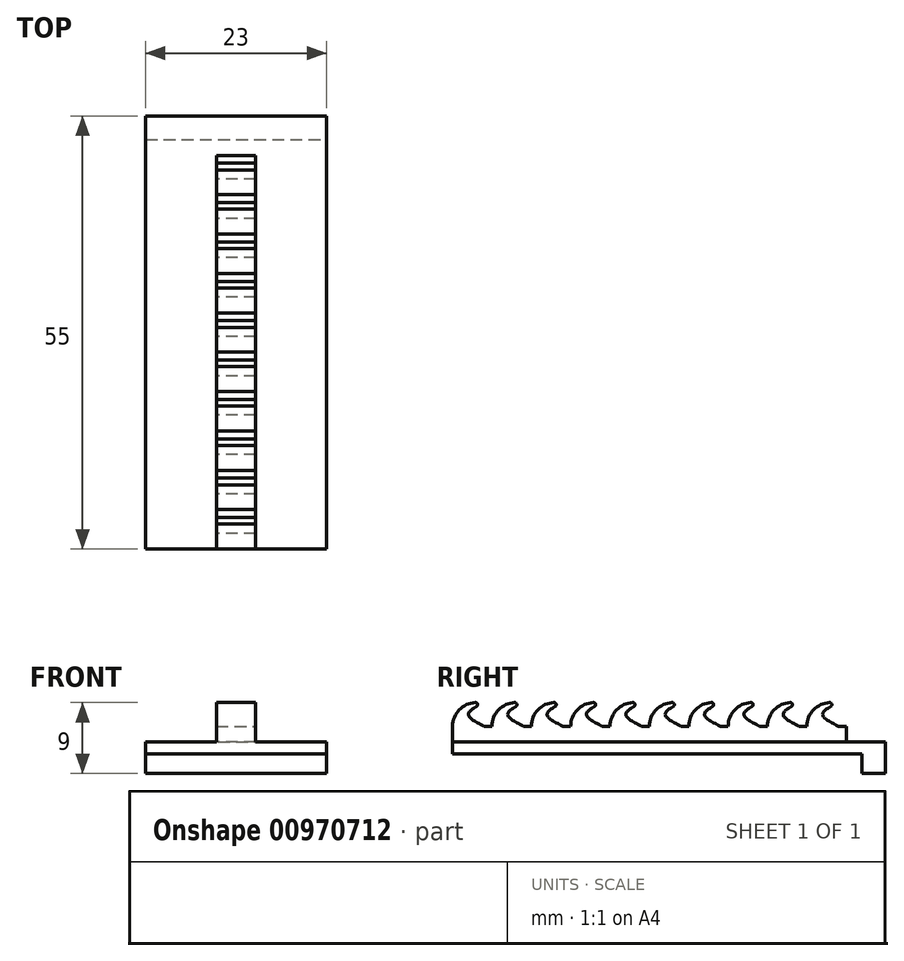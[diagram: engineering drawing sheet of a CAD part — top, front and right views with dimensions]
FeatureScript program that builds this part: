
annotation { "Feature Type Name" : "Feature", "Feature Type Description" : "" }
export const myFeature = defineFeature(function(context is Context, id is Id, definition is map)
    precondition{}
    {
        {
            var Q0;
            Q0=qCreatedBy(makeId("Top.planeOp"),FACE);
            var sketch = newSketch(context, id + "F0", { "sketchPlane" : qUnion([Q0])});
            skLineSegment(sketch, "E0.bottom", {"start": v(-13.13, 25.1) * mm, "end": v(9.87, 25.1) * mm});
            skLineSegment(sketch, "E0.top", {"start": v(-13.13, -26.9) * mm, "end": v(9.87, -26.9) * mm});
            skLineSegment(sketch, "E0.left", {"start": v(-13.13, 25.1) * mm, "end": v(-13.13, -26.9) * mm});
            skLineSegment(sketch, "E0.right", {"start": v(9.87, 25.1) * mm, "end": v(9.87, -26.9) * mm});
            skSolve(sketch);
        }
        {
            var Q0;
            Q0=makeQuery(id+"F0.imprint","IMPRINT",FACE,{"disambiguationData":[TD([[makeQuery(id+"F0.imprint","IMPRINT",EDGE,{"derivedFrom":sQuery(id+"F0.wireOp",EDGE,"E0.bottom")}),-1.0]])]});
            extrude(context, id + "F1", {"entities" : qUnion([Q0]), "depth" : 1.5 * mm, "offsetDistance" : 25 * mm});
        }
        {
            var Q0;
            Q0=makeQuery(id+"F1.opExtrude","SWEPT_FACE",FACE,{"disambiguationData":[OSD([sQuery(id+"F0.wireOp",EDGE,"E0.bottom")])]});
            var sketch = newSketch(context, id + "F2", { "sketchPlane" : qUnion([Q0])});
            skLineSegment(sketch, "E1.bottom", {"start": v(-9.87, 1.5) * mm, "end": v(13.13, 1.5) * mm});
            skLineSegment(sketch, "E1.top", {"start": v(-9.87, -2.5) * mm, "end": v(13.13, -2.5) * mm});
            skLineSegment(sketch, "E1.left", {"start": v(-9.87, 1.5) * mm, "end": v(-9.87, -2.5) * mm});
            skLineSegment(sketch, "E1.right", {"start": v(13.13, 1.5) * mm, "end": v(13.13, -2.5) * mm});
            skSolve(sketch);
        }
        {
            var Q0;
            Q0 = qSketchRegion(id + "F2", true);
            extrude(context, id + "F3", {"entities" : qUnion([Q0]), "operationType" : NewBodyOperationType.ADD, "depth" : 3 * mm, "offsetDistance" : 25 * mm});
        }
        {
            var Q0;
            Q0=makeQuery(id+"F3.boolean.opBoolean","MERGE",FACE,{"derivedFrom":[makeQuery(id+"F1.opExtrude","CAP_FACE",FACE,{"disambiguationData":[OSD([sQuery(id+"F0.wireOp",EDGE,"E0.bottom"),sQuery(id+"F0.wireOp",EDGE,"E0.top"),sQuery(id+"F0.wireOp",EDGE,"E0.left"),sQuery(id+"F0.wireOp",EDGE,"E0.right")])],"isStart":false}),makeQuery(id+"F3.opExtrude","SWEPT_FACE",FACE,{"disambiguationData":[OSD([sQuery(id+"F2.wireOp",EDGE,"E1.bottom")])]})]});
            var sketch = newSketch(context, id + "F4", { "sketchPlane" : qUnion([Q0])});
            skLineSegment(sketch, "E2", {"start": v(-1.63, -26.9) * mm, "end": v(-4.13, -26.9) * mm});
            skLineSegment(sketch, "E3", {"start": v(-1.63, -26.9) * mm, "end": v(0.87, -26.9) * mm});
            skLineSegment(sketch, "E4.bottom", {"start": v(-4.13, -26.9) * mm, "end": v(0, -26.9) * mm});
            skLineSegment(sketch, "E4.left", {"start": v(-4.13, -26.9) * mm, "end": v(-4.13, 23.1) * mm});
            skLineSegment(sketch, "E5", {"start": v(0.87, -26.9) * mm, "end": v(0.87, 23.1) * mm});
            skLineSegment(sketch, "E6", {"start": v(0.87, 23.1) * mm, "end": v(-4.13, 23.1) * mm});
            skSolve(sketch);
        }
        {
            var Q0;
            Q0 = qSketchRegion(id + "F4", true);
            extrude(context, id + "F5", {"entities" : qUnion([Q0]), "operationType" : NewBodyOperationType.ADD, "depth" : 2 * mm, "offsetDistance" : 25 * mm});
        }
        {
            var Q0;
            Q0=makeQuery(id+"F5.opExtrude","CAP_FACE",FACE,{"disambiguationData":[OSD([sQuery(id+"F4.wireOp",EDGE,"E4.bottom"),sQuery(id+"F4.wireOp",EDGE,"E4.top"),sQuery(id+"F4.wireOp",EDGE,"E4.left"),sQuery(id+"F4.wireOp",EDGE,"E4.right")])],"isStart":false});
            var sketch = newSketch(context, id + "F6", { "sketchPlane" : qUnion([Q0])});
            skLineSegment(sketch, "E7.bottom", {"start": v(-4.13, -26.9) * mm, "end": v(0.87, -26.9) * mm});
            skLineSegment(sketch, "E7.top", {"start": v(-4.13, -21.9) * mm, "end": v(0.87, -21.9) * mm});
            skLineSegment(sketch, "E7.left", {"start": v(-4.13, -26.9) * mm, "end": v(-4.13, -21.9) * mm});
            skLineSegment(sketch, "E7.right", {"start": v(0.87, -26.9) * mm, "end": v(0.87, -21.9) * mm});
            skLineSegment(sketch, "E8.top", {"start": v(-4.13, -16.9) * mm, "end": v(0.87, -16.9) * mm});
            skLineSegment(sketch, "E8.left", {"start": v(-4.13, -21.9) * mm, "end": v(-4.13, -16.9) * mm});
            skLineSegment(sketch, "E8.right", {"start": v(0.87, -21.9) * mm, "end": v(0.87, -16.9) * mm});
            skLineSegment(sketch, "E9", {"start": v(0.87, -16.9) * mm, "end": v(0.87, -11.9) * mm});
            skLineSegment(sketch, "E10", {"start": v(0.87, -11.9) * mm, "end": v(0.87, -6.9) * mm});
            skPoint(sketch, "E11", {"position": v(0.87, -1.9) * mm});
            skPoint(sketch, "E12", {"position": v(0.87, 3.1) * mm});
            skPoint(sketch, "E13", {"position": v(0.87, 8.1) * mm});
            skPoint(sketch, "E14", {"position": v(0.87, 13.1) * mm});
            skPoint(sketch, "E15", {"position": v(0.87, 18.1) * mm});
            skPoint(sketch, "E16", {"position": v(0.87, 23.1) * mm});
            skLineSegment(sketch, "E17.top", {"start": v(-4.13, -11.9) * mm, "end": v(0.87, -11.9) * mm});
            skLineSegment(sketch, "E17.left", {"start": v(-4.13, -16.9) * mm, "end": v(-4.13, -11.9) * mm});
            skLineSegment(sketch, "E18.top", {"start": v(-4.13, -6.9) * mm, "end": v(0.87, -6.9) * mm});
            skLineSegment(sketch, "E18.left", {"start": v(-4.13, -11.9) * mm, "end": v(-4.13, -6.9) * mm});
            skLineSegment(sketch, "E19.top", {"start": v(-4.13, -1.9) * mm, "end": v(0.87, -1.9) * mm});
            skLineSegment(sketch, "E19.left", {"start": v(-4.13, -6.9) * mm, "end": v(-4.13, -1.9) * mm});
            skLineSegment(sketch, "E19.right", {"start": v(0.87, -6.9) * mm, "end": v(0.87, -1.9) * mm});
            skLineSegment(sketch, "E20.top", {"start": v(-4.13, 3.1) * mm, "end": v(0.87, 3.1) * mm});
            skLineSegment(sketch, "E20.left", {"start": v(-4.13, -1.9) * mm, "end": v(-4.13, 3.1) * mm});
            skLineSegment(sketch, "E20.right", {"start": v(0.87, -1.9) * mm, "end": v(0.87, 3.1) * mm});
            skLineSegment(sketch, "E21.top", {"start": v(-4.13, 8.1) * mm, "end": v(0.87, 8.1) * mm});
            skLineSegment(sketch, "E21.left", {"start": v(-4.13, 3.1) * mm, "end": v(-4.13, 8.1) * mm});
            skLineSegment(sketch, "E21.right", {"start": v(0.87, 3.1) * mm, "end": v(0.87, 8.1) * mm});
            skLineSegment(sketch, "E22.top", {"start": v(-4.13, 13.1) * mm, "end": v(0.87, 13.1) * mm});
            skLineSegment(sketch, "E22.left", {"start": v(-4.13, 8.1) * mm, "end": v(-4.13, 13.1) * mm});
            skLineSegment(sketch, "E22.right", {"start": v(0.87, 8.1) * mm, "end": v(0.87, 13.1) * mm});
            skLineSegment(sketch, "E23.top", {"start": v(-4.13, 18.1) * mm, "end": v(0.87, 18.1) * mm});
            skLineSegment(sketch, "E23.left", {"start": v(-4.13, 13.1) * mm, "end": v(-4.13, 18.1) * mm});
            skLineSegment(sketch, "E23.right", {"start": v(0.87, 13.1) * mm, "end": v(0.87, 18.1) * mm});
            skLineSegment(sketch, "E24.top", {"start": v(-4.13, 23.1) * mm, "end": v(0.87, 23.1) * mm});
            skLineSegment(sketch, "E24.left", {"start": v(-4.13, 18.1) * mm, "end": v(-4.13, 23.1) * mm});
            skLineSegment(sketch, "E24.right", {"start": v(0.87, 18.1) * mm, "end": v(0.87, 23.1) * mm});
            skLineSegment(sketch, "E25", {"start": v(-4.13, -22.9) * mm, "end": v(0.87, -22.9) * mm});
            skLineSegment(sketch, "E26", {"start": v(-4.13, -17.9) * mm, "end": v(0.87, -17.9) * mm});
            skLineSegment(sketch, "E27", {"start": v(-4.13, 22.1) * mm, "end": v(0.87, 22.1) * mm});
            skLineSegment(sketch, "E28", {"start": v(-4.13, 17.1) * mm, "end": v(0.87, 17.1) * mm});
            skLineSegment(sketch, "E29", {"start": v(0.87, 17.1) * mm, "end": v(0.87, 12.1) * mm});
            skLineSegment(sketch, "E30", {"start": v(0.87, 12.1) * mm, "end": v(-4.13, 12.1) * mm});
            skLineSegment(sketch, "E31", {"start": v(-4.13, 12.1) * mm, "end": v(-4.13, 7.1) * mm});
            skLineSegment(sketch, "E32", {"start": v(-4.13, 7.1) * mm, "end": v(0.87, 7.1) * mm});
            skLineSegment(sketch, "E33", {"start": v(0.87, 7.1) * mm, "end": v(0.87, 2.1) * mm});
            skLineSegment(sketch, "E34", {"start": v(0.87, 2.1) * mm, "end": v(-4.13, 2.1) * mm});
            skLineSegment(sketch, "E35", {"start": v(-4.13, 2.1) * mm, "end": v(-4.13, -2.9) * mm});
            skLineSegment(sketch, "E36", {"start": v(-4.13, -2.9) * mm, "end": v(0.87, -2.9) * mm});
            skLineSegment(sketch, "E37", {"start": v(0.87, 2.1) * mm, "end": v(0.87, -2.9) * mm});
            skLineSegment(sketch, "E38", {"start": v(0.87, -2.9) * mm, "end": v(0.87, -7.9) * mm});
            skLineSegment(sketch, "E39", {"start": v(0.87, -7.9) * mm, "end": v(-4.13, -7.9) * mm});
            skLineSegment(sketch, "E40", {"start": v(-4.13, -7.9) * mm, "end": v(-4.13, -12.9) * mm});
            skLineSegment(sketch, "E41", {"start": v(-4.13, -12.9) * mm, "end": v(0.87, -12.9) * mm});
            skSolve(sketch);
        }
        {
            var Q0;
            {var subQ0=sQuery(id+"F6.wireOp",EDGE,"E7.bottom");Q0=makeQuery(id+"F6.imprint","IMPRINT",FACE,{"disambiguationData":[TD([[makeQuery(id+"F6.imprint","IMPRINT",EDGE,{"derivedFrom":subQ0}),1.0]])]});}
            var Q1;
            {var subQ0=sQuery(id+"F6.wireOp",EDGE,"E7.top");Q1=makeQuery(id+"F6.imprint","IMPRINT",FACE,{"disambiguationData":[TD([[makeQuery(id+"F6.imprint","IMPRINT",EDGE,{"derivedFrom":subQ0}),1.0]])]});}
            var Q2;
            {var subQ0=sQuery(id+"F6.wireOp",EDGE,"E8.top");Q2=makeQuery(id+"F6.imprint","IMPRINT",FACE,{"disambiguationData":[TD([[makeQuery(id+"F6.imprint","IMPRINT",EDGE,{"derivedFrom":subQ0}),1.0]])]});}
            var Q3;
            {var subQ0=sQuery(id+"F6.wireOp",EDGE,"E17.top");Q3=makeQuery(id+"F6.imprint","IMPRINT",FACE,{"disambiguationData":[TD([[makeQuery(id+"F6.imprint","IMPRINT",EDGE,{"derivedFrom":subQ0}),1.0]])]});}
            var Q4;
            {var subQ0=sQuery(id+"F6.wireOp",EDGE,"E18.top");Q4=makeQuery(id+"F6.imprint","IMPRINT",FACE,{"disambiguationData":[TD([[makeQuery(id+"F6.imprint","IMPRINT",EDGE,{"derivedFrom":subQ0}),1.0]])]});}
            var Q5;
            {var subQ0=sQuery(id+"F6.wireOp",EDGE,"E19.top");Q5=makeQuery(id+"F6.imprint","IMPRINT",FACE,{"disambiguationData":[TD([[makeQuery(id+"F6.imprint","IMPRINT",EDGE,{"derivedFrom":subQ0}),1.0]])]});}
            var Q6;
            {var subQ0=sQuery(id+"F6.wireOp",EDGE,"E20.top");Q6=makeQuery(id+"F6.imprint","IMPRINT",FACE,{"disambiguationData":[TD([[makeQuery(id+"F6.imprint","IMPRINT",EDGE,{"derivedFrom":subQ0}),1.0]])]});}
            var Q7;
            {var subQ0=sQuery(id+"F6.wireOp",EDGE,"E19.top");Q7=makeQuery(id+"F6.imprint","IMPRINT",FACE,{"disambiguationData":[TD([[makeQuery(id+"F6.imprint","IMPRINT",EDGE,{"derivedFrom":subQ0}),1.0]])]});}
            var Q8;
            {var subQ0=sQuery(id+"F6.wireOp",EDGE,"E20.top");Q8=makeQuery(id+"F6.imprint","IMPRINT",FACE,{"disambiguationData":[TD([[makeQuery(id+"F6.imprint","IMPRINT",EDGE,{"derivedFrom":subQ0}),1.0]])]});}
            var Q9;
            {var subQ0=sQuery(id+"F6.wireOp",EDGE,"E21.top");Q9=makeQuery(id+"F6.imprint","IMPRINT",FACE,{"disambiguationData":[TD([[makeQuery(id+"F6.imprint","IMPRINT",EDGE,{"derivedFrom":subQ0}),1.0]])]});}
            var Q10;
            {var subQ0=sQuery(id+"F6.wireOp",EDGE,"E22.top");Q10=makeQuery(id+"F6.imprint","IMPRINT",FACE,{"disambiguationData":[TD([[makeQuery(id+"F6.imprint","IMPRINT",EDGE,{"derivedFrom":subQ0}),1.0]])]});}
            var Q11;
            {var subQ0=sQuery(id+"F6.wireOp",EDGE,"E23.top");Q11=makeQuery(id+"F6.imprint","IMPRINT",FACE,{"disambiguationData":[TD([[makeQuery(id+"F6.imprint","IMPRINT",EDGE,{"derivedFrom":subQ0}),1.0]])]});}
            extrude(context, id + "F7", {"entities" : qUnion([Q0, Q1, Q2, Q3, Q4, Q5, Q6, Q7, Q8, Q9, Q10, Q11]), "operationType" : NewBodyOperationType.ADD, "depth" : 3 * mm, "offsetDistance" : 25 * mm});
        }
        {
            var Q0;
            Q0=makeQuery(id+"F7.boolean.opBoolean","MERGE",FACE,{"derivedFrom":[makeQuery(id+"F5.opExtrude","SWEPT_FACE",FACE,{"disambiguationData":[OSD([sQuery(id+"F4.wireOp",EDGE,"E4.left")])]}),makeQuery(id+"F7.opExtrude","SWEPT_FACE",FACE,{"disambiguationData":[OSD([sQuery(id+"F6.wireOp",EDGE,"E7.left")])]}),makeQuery(id+"F7.opExtrude","SWEPT_FACE",FACE,{"disambiguationData":[OSD([sQuery(id+"F6.wireOp",EDGE,"E8.left")])]}),makeQuery(id+"F7.opExtrude","SWEPT_FACE",FACE,{"disambiguationData":[OSD([sQuery(id+"F6.wireOp",EDGE,"E17.left")])]}),makeQuery(id+"F7.opExtrude","SWEPT_FACE",FACE,{"disambiguationData":[OSD([sQuery(id+"F6.wireOp",EDGE,"E18.left")])]}),makeQuery(id+"F7.opExtrude","SWEPT_FACE",FACE,{"disambiguationData":[OSD([sQuery(id+"F6.wireOp",EDGE,"E19.left")])]}),makeQuery(id+"F7.opExtrude","SWEPT_FACE",FACE,{"disambiguationData":[OSD([sQuery(id+"F6.wireOp",EDGE,"E20.left")])]}),makeQuery(id+"F7.opExtrude","SWEPT_FACE",FACE,{"disambiguationData":[OSD([sQuery(id+"F6.wireOp",EDGE,"E21.left")])]}),makeQuery(id+"F7.opExtrude","SWEPT_FACE",FACE,{"disambiguationData":[OSD([sQuery(id+"F6.wireOp",EDGE,"E22.left")])]}),makeQuery(id+"F7.opExtrude","SWEPT_FACE",FACE,{"disambiguationData":[OSD([sQuery(id+"F6.wireOp",EDGE,"E23.left")])]}),makeQuery(id+"F7.opExtrude","SWEPT_FACE",FACE,{"disambiguationData":[OSD([sQuery(id+"F6.wireOp",EDGE,"E24.left")])]})]});
            var sketch = newSketch(context, id + "F8", { "sketchPlane" : qUnion([Q0])});
            skPoint(sketch, "E42", {"position": v(24.9, 5) * mm});
            skPoint(sketch, "E42.positionSnap0", {"position": v(24.9, 6.5) * mm});
            skPoint(sketch, "E42.positionSnap1", {"position": v(22.9, 5) * mm});
            skFitSpline(sketch, "E43", {"points": [v(22.9, 3.5) * mm, v(24.9, 5) * mm, v(22.9, 6.5) * mm], "startDerivative": vector(6, 3) * mm, "endDerivative": vector(-6, 3) * mm});
            skPoint(sketch, "E44", {"position": v(17.9, 5) * mm});
            skPoint(sketch, "E45", {"position": v(19.9, 5) * mm});
            skPoint(sketch, "E45.positionSnap0", {"position": v(19.9, 6.5) * mm});
            skPoint(sketch, "E46", {"position": v(14.9, 5) * mm});
            skPoint(sketch, "E46.positionSnap0", {"position": v(14.9, 6.5) * mm});
            skPoint(sketch, "E46.positionSnap1", {"position": v(12.9, 5) * mm});
            skPoint(sketch, "E47", {"position": v(7.9, 5) * mm});
            skPoint(sketch, "E48", {"position": v(9.9, 5) * mm});
            skPoint(sketch, "E48.positionSnap0", {"position": v(9.9, 6.5) * mm});
            skPoint(sketch, "E49", {"position": v(4.9, 5) * mm});
            skPoint(sketch, "E49.positionSnap0", {"position": v(4.9, 6.5) * mm});
            skPoint(sketch, "E49.positionSnap1", {"position": v(2.9, 5) * mm});
            skPoint(sketch, "E50", {"position": v(-0.1, 5) * mm});
            skPoint(sketch, "E50.positionSnap0", {"position": v(-2.1, 5) * mm});
            skPoint(sketch, "E50.positionSnap1", {"position": v(-0.1, 6.5) * mm});
            skPoint(sketch, "E51", {"position": v(-5.1, 5) * mm});
            skPoint(sketch, "E51.positionSnap0", {"position": v(-5.1, 6.5) * mm});
            skPoint(sketch, "E51.positionSnap1", {"position": v(1.9, 5) * mm});
            skPoint(sketch, "E52.positionSnap1", {"position": v(-7.1, 5) * mm});
            skPoint(sketch, "E53", {"position": v(-10.1, 5) * mm});
            skPoint(sketch, "E53.positionSnap0", {"position": v(-10.1, 6.5) * mm});
            skPoint(sketch, "E53.positionSnap1", {"position": v(-12.1, 5) * mm});
            skPoint(sketch, "E54", {"position": v(-20.1, 5) * mm});
            skPoint(sketch, "E54.positionSnap0", {"position": v(-20.1, 6.5) * mm});
            skPoint(sketch, "E54.positionSnap1", {"position": v(-22.1, 5) * mm});
            skPoint(sketch, "E55", {"position": v(-15.1, 5) * mm});
            skPoint(sketch, "E55.positionSnap0", {"position": v(-15.1, 6.5) * mm});
            skPoint(sketch, "E55.positionSnap1", {"position": v(-17.1, 5) * mm});
            skFitSpline(sketch, "E56", {"points": [v(17.9, 3.5) * mm, v(19.9, 5) * mm, v(17.9, 6.5) * mm], "startDerivative": vector(6, 3) * mm, "endDerivative": vector(-6, 3) * mm});
            skFitSpline(sketch, "E57", {"points": [v(12.9, 3.5) * mm, v(14.9, 5) * mm, v(12.9, 6.5) * mm], "startDerivative": vector(6, 3) * mm, "endDerivative": vector(-6, 3) * mm});
            skFitSpline(sketch, "E58", {"points": [v(7.9, 3.5) * mm, v(9.9, 5) * mm, v(7.9, 6.5) * mm], "startDerivative": vector(6, 3) * mm, "endDerivative": vector(-6, 3) * mm});
            skFitSpline(sketch, "E59", {"points": [v(2.9, 3.5) * mm, v(4.9, 5) * mm, v(2.9, 6.5) * mm], "startDerivative": vector(6, 3) * mm, "endDerivative": vector(-6, 3) * mm});
            skFitSpline(sketch, "E60", {"points": [v(-2.1, 3.5) * mm, v(-0.1, 5) * mm, v(-2.1, 6.5) * mm], "startDerivative": vector(6, 3) * mm, "endDerivative": vector(-6, 3) * mm});
            skFitSpline(sketch, "E61", {"points": [v(-2.1, 3.5) * mm, v(-0.1, 5) * mm, v(-2.1, 6.5) * mm], "startDerivative": vector(6, 3) * mm, "endDerivative": vector(-6, 3) * mm});
            skFitSpline(sketch, "E62", {"points": [v(-7.1, 3.5) * mm, v(-5.1, 5) * mm, v(-7.1, 6.5) * mm], "startDerivative": vector(6, 3) * mm, "endDerivative": vector(-6, 3) * mm});
            skFitSpline(sketch, "E63", {"points": [v(-12.1, 3.5) * mm, v(-10.1, 5) * mm, v(-12.1, 6.5) * mm], "startDerivative": vector(6, 3) * mm, "endDerivative": vector(-6, 3) * mm});
            skFitSpline(sketch, "E64", {"points": [v(-17.1, 3.5) * mm, v(-15.1, 5) * mm, v(-17.1, 6.5) * mm], "startDerivative": vector(6, 3) * mm, "endDerivative": vector(-6, 3) * mm});
            skFitSpline(sketch, "E65", {"points": [v(-22.1, 3.5) * mm, v(-20.1, 5) * mm, v(-22.1, 6.5) * mm], "startDerivative": vector(6, 3) * mm, "endDerivative": vector(-6, 3) * mm});
            skLineSegment(sketch, "E66", {"start": v(-22.1, 3.5) * mm, "end": v(-22.1, 6.5) * mm});
            skLineSegment(sketch, "E67", {"start": v(-17.1, 3.5) * mm, "end": v(-17.1, 6.5) * mm});
            skLineSegment(sketch, "E68", {"start": v(-12.1, 3.5) * mm, "end": v(-12.1, 6.5) * mm});
            skLineSegment(sketch, "E69", {"start": v(-7.1, 3.5) * mm, "end": v(-7.1, 6.5) * mm});
            skLineSegment(sketch, "E70", {"start": v(-2.1, 3.5) * mm, "end": v(-2.1, 6.5) * mm});
            skLineSegment(sketch, "E71", {"start": v(1.9, 3.5) * mm, "end": v(1.9, 6.5) * mm});
            skLineSegment(sketch, "E72", {"start": v(2.9, 3.5) * mm, "end": v(2.9, 6.5) * mm});
            skLineSegment(sketch, "E73", {"start": v(7.9, 3.5) * mm, "end": v(7.9, 6.5) * mm});
            skLineSegment(sketch, "E74", {"start": v(12.9, 3.5) * mm, "end": v(12.9, 6.5) * mm});
            skLineSegment(sketch, "E75", {"start": v(17.9, 3.5) * mm, "end": v(17.9, 6.5) * mm});
            skLineSegment(sketch, "E76", {"start": v(22.9, 3.5) * mm, "end": v(22.9, 6.5) * mm});
            skSolve(sketch);
        }
        {
            var Q0;
            Q0 = qSketchRegion(id + "F8", true);
            var Q1;
            Q1=makeQuery(id+"F8.imprint","IMPRINT",FACE,{"disambiguationData":[TD([[makeQuery(id+"F8.imprint","IMPRINT",EDGE,{"derivedFrom":sQuery(id+"F8.wireOp",EDGE,"E43")}),1.0]])]});
            extrude(context, id + "F9", {"entities" : qUnion([Q0, Q1]), "operationType" : NewBodyOperationType.REMOVE, "oppositeDirection" : true, "depth" : 5.1 * mm, "offsetDistance" : 25 * mm});
        }
        {
            var Q0;
            Q0=makeQuery(id+"F7.opExtrude","CAP_EDGE",EDGE,{"disambiguationData":[OSD([sQuery(id+"F6.wireOp",EDGE,"E7.bottom")])],"isStart":false});
            var Q1;
            Q1=makeQuery(id+"F7.opExtrude","CAP_EDGE",EDGE,{"disambiguationData":[OSD([sQuery(id+"F6.wireOp",EDGE,"E7.top")])],"isStart":false});
            var Q2;
            Q2=makeQuery(id+"F7.opExtrude","CAP_EDGE",EDGE,{"disambiguationData":[OSD([sQuery(id+"F6.wireOp",EDGE,"E8.top")])],"isStart":false});
            var Q3;
            Q3=makeQuery(id+"F7.opExtrude","CAP_EDGE",EDGE,{"disambiguationData":[OSD([sQuery(id+"F6.wireOp",EDGE,"E17.top")])],"isStart":false});
            var Q4;
            Q4=makeQuery(id+"F7.opExtrude","CAP_EDGE",EDGE,{"disambiguationData":[OSD([sQuery(id+"F6.wireOp",EDGE,"E18.top")])],"isStart":false});
            var Q5;
            Q5=makeQuery(id+"F7.opExtrude","CAP_EDGE",EDGE,{"disambiguationData":[OSD([sQuery(id+"F6.wireOp",EDGE,"E19.top")])],"isStart":false});
            var Q6;
            Q6=makeQuery(id+"F7.opExtrude","CAP_EDGE",EDGE,{"disambiguationData":[OSD([sQuery(id+"F6.wireOp",EDGE,"E20.top")])],"isStart":false});
            var Q7;
            Q7=makeQuery(id+"F7.opExtrude","CAP_EDGE",EDGE,{"disambiguationData":[OSD([sQuery(id+"F6.wireOp",EDGE,"E19.top")])],"isStart":false});
            var Q8;
            Q8=makeQuery(id+"F7.opExtrude","CAP_EDGE",EDGE,{"disambiguationData":[OSD([sQuery(id+"F6.wireOp",EDGE,"E20.top")])],"isStart":false});
            var Q9;
            Q9=makeQuery(id+"F7.opExtrude","CAP_EDGE",EDGE,{"disambiguationData":[OSD([sQuery(id+"F6.wireOp",EDGE,"E21.top")])],"isStart":false});
            var Q10;
            Q10=makeQuery(id+"F7.opExtrude","CAP_EDGE",EDGE,{"disambiguationData":[OSD([sQuery(id+"F6.wireOp",EDGE,"E22.top")])],"isStart":false});
            var Q11;
            Q11=makeQuery(id+"F7.opExtrude","CAP_EDGE",EDGE,{"disambiguationData":[OSD([sQuery(id+"F6.wireOp",EDGE,"E23.top")])],"isStart":false});
            fillet(context, id + "F10", {"entities" : qUnion([Q0, Q1, Q2, Q3, Q4, Q5, Q6, Q7, Q8, Q9, Q10, Q11]), "radius" : 3 * mm, "tangentPropagation" : true, "allowEdgeOverflow" : false});
        }
        {
            var Q0;
            Q0=makeQuery(id+"F9.boolean.opBoolean","MERGE",EDGE,{"derivedFrom":[makeQuery(id+"F7.opExtrude","CAP_EDGE",EDGE,{"disambiguationData":[OSD([sQuery(id+"F6.wireOp",EDGE,"E25")])],"isStart":false})],"fromTools":[makeQuery(id+"F9.opExtrude","SWEPT_EDGE",EDGE,{"disambiguationData":[OSD([sQuery(id+"F6.wireOp",EDGE,"E7.left"),sQuery(id+"F8.wireOp",EDGE,"E43"),sQuery(id+"F8.wireOp",EDGE,"E76")])]})]});
            var Q1;
            Q1=makeQuery(id+"F9.boolean.opBoolean","MERGE",EDGE,{"derivedFrom":[makeQuery(id+"F7.opExtrude","CAP_EDGE",EDGE,{"disambiguationData":[OSD([sQuery(id+"F6.wireOp",EDGE,"E27")])],"isStart":false})],"fromTools":[makeQuery(id+"F9.opExtrude","SWEPT_EDGE",EDGE,{"disambiguationData":[OSD([sQuery(id+"F6.wireOp",EDGE,"E24.left"),sQuery(id+"F8.wireOp",EDGE,"E65"),sQuery(id+"F8.wireOp",EDGE,"E66")])]})]});
            var Q2;
            Q2=makeQuery(id+"F9.boolean.opBoolean","MERGE",EDGE,{"derivedFrom":[makeQuery(id+"F7.opExtrude","CAP_EDGE",EDGE,{"disambiguationData":[OSD([sQuery(id+"F6.wireOp",EDGE,"E28")])],"isStart":false})],"fromTools":[makeQuery(id+"F9.opExtrude","SWEPT_EDGE",EDGE,{"disambiguationData":[OSD([sQuery(id+"F6.wireOp",EDGE,"E23.left"),sQuery(id+"F8.wireOp",EDGE,"E64"),sQuery(id+"F8.wireOp",EDGE,"E67")])]})]});
            var Q3;
            Q3=makeQuery(id+"F9.boolean.opBoolean","MERGE",EDGE,{"derivedFrom":[makeQuery(id+"F7.opExtrude","CAP_EDGE",EDGE,{"disambiguationData":[OSD([sQuery(id+"F6.wireOp",EDGE,"E30")])],"isStart":false})],"fromTools":[makeQuery(id+"F9.opExtrude","SWEPT_EDGE",EDGE,{"disambiguationData":[OSD([sQuery(id+"F6.wireOp",EDGE,"E22.left"),sQuery(id+"F8.wireOp",EDGE,"E63"),sQuery(id+"F8.wireOp",EDGE,"E68")])]})]});
            var Q4;
            Q4=makeQuery(id+"F9.boolean.opBoolean","MERGE",EDGE,{"derivedFrom":[makeQuery(id+"F7.opExtrude","CAP_EDGE",EDGE,{"disambiguationData":[OSD([sQuery(id+"F6.wireOp",EDGE,"E32")])],"isStart":false})],"fromTools":[makeQuery(id+"F9.opExtrude","SWEPT_EDGE",EDGE,{"disambiguationData":[OSD([sQuery(id+"F6.wireOp",EDGE,"E21.left"),sQuery(id+"F8.wireOp",EDGE,"E62"),sQuery(id+"F8.wireOp",EDGE,"E69")])]})]});
            var Q5;
            Q5=makeQuery(id+"F9.boolean.opBoolean","MERGE",EDGE,{"derivedFrom":[makeQuery(id+"F7.opExtrude","CAP_EDGE",EDGE,{"disambiguationData":[OSD([sQuery(id+"F6.wireOp",EDGE,"E36")])],"isStart":false})],"fromTools":[makeQuery(id+"F9.opExtrude","SWEPT_EDGE",EDGE,{"disambiguationData":[OSD([sQuery(id+"F6.wireOp",EDGE,"E20.left"),sQuery(id+"F8.wireOp",EDGE,"86b174c8-a1d0-4a33-b58b-315386d1a98e"),sQuery(id+"F8.wireOp",EDGE,"E71")])]})]});
            var Q6;
            Q6=makeQuery(id+"F9.boolean.opBoolean","MERGE",EDGE,{"derivedFrom":[makeQuery(id+"F7.opExtrude","CAP_EDGE",EDGE,{"disambiguationData":[OSD([sQuery(id+"F6.wireOp",EDGE,"E36")])],"isStart":false})],"fromTools":[makeQuery(id+"F9.opExtrude","SWEPT_EDGE",EDGE,{"disambiguationData":[OSD([sQuery(id+"F6.wireOp",EDGE,"E19.left"),sQuery(id+"F8.wireOp",EDGE,"E59"),sQuery(id+"F8.wireOp",EDGE,"E72")])]})]});
            var Q7;
            Q7=makeQuery(id+"F9.boolean.opBoolean","MERGE",EDGE,{"derivedFrom":[makeQuery(id+"F7.opExtrude","CAP_EDGE",EDGE,{"disambiguationData":[OSD([sQuery(id+"F6.wireOp",EDGE,"E39")])],"isStart":false})],"fromTools":[makeQuery(id+"F9.opExtrude","SWEPT_EDGE",EDGE,{"disambiguationData":[OSD([sQuery(id+"F6.wireOp",EDGE,"E18.left"),sQuery(id+"F8.wireOp",EDGE,"E58"),sQuery(id+"F8.wireOp",EDGE,"E73")])]})]});
            var Q8;
            Q8=makeQuery(id+"F9.boolean.opBoolean","MERGE",EDGE,{"derivedFrom":[makeQuery(id+"F7.opExtrude","CAP_EDGE",EDGE,{"disambiguationData":[OSD([sQuery(id+"F6.wireOp",EDGE,"E41")])],"isStart":false})],"fromTools":[makeQuery(id+"F9.opExtrude","SWEPT_EDGE",EDGE,{"disambiguationData":[OSD([sQuery(id+"F6.wireOp",EDGE,"E17.left"),sQuery(id+"F8.wireOp",EDGE,"E57"),sQuery(id+"F8.wireOp",EDGE,"E74")])]})]});
            var Q9;
            Q9=makeQuery(id+"F9.boolean.opBoolean","MERGE",EDGE,{"derivedFrom":[makeQuery(id+"F7.opExtrude","CAP_EDGE",EDGE,{"disambiguationData":[OSD([sQuery(id+"F6.wireOp",EDGE,"E26")])],"isStart":false})],"fromTools":[makeQuery(id+"F9.opExtrude","SWEPT_EDGE",EDGE,{"disambiguationData":[OSD([sQuery(id+"F6.wireOp",EDGE,"E8.left"),sQuery(id+"F8.wireOp",EDGE,"E56"),sQuery(id+"F8.wireOp",EDGE,"E75")])]})]});
            var Q10;
            Q10=makeQuery(id+"F9.boolean.opBoolean","MERGE",EDGE,{"derivedFrom":[makeQuery(id+"F7.opExtrude","CAP_EDGE",EDGE,{"disambiguationData":[OSD([sQuery(id+"F6.wireOp",EDGE,"E34")])],"isStart":false})],"fromTools":[makeQuery(id+"F9.opExtrude","SWEPT_EDGE",EDGE,{"disambiguationData":[OSD([sQuery(id+"F6.wireOp",EDGE,"E20.left"),sQuery(id+"F8.wireOp",EDGE,"E60"),sQuery(id+"F8.wireOp",EDGE,"E70")])]})]});
            var Q11;
            Q11=makeQuery(id+"F9.boolean.opBoolean","MERGE",EDGE,{"derivedFrom":[makeQuery(id+"F7.opExtrude","CAP_EDGE",EDGE,{"disambiguationData":[OSD([sQuery(id+"F6.wireOp",EDGE,"E34")])],"isStart":false})],"fromTools":[makeQuery(id+"F9.opExtrude","SWEPT_EDGE",EDGE,{"disambiguationData":[OSD([sQuery(id+"F6.wireOp",EDGE,"E20.left"),sQuery(id+"F8.wireOp",EDGE,"E60"),sQuery(id+"F8.wireOp",EDGE,"E70")])]})]});
            fillet(context, id + "F11", {"entities" : qUnion([Q0, Q1, Q2, Q3, Q4, Q5, Q6, Q7, Q8, Q9, Q10, Q11]), "radius" : 0.27 * mm, "tangentPropagation" : true, "allowEdgeOverflow" : false});
        }
    });
